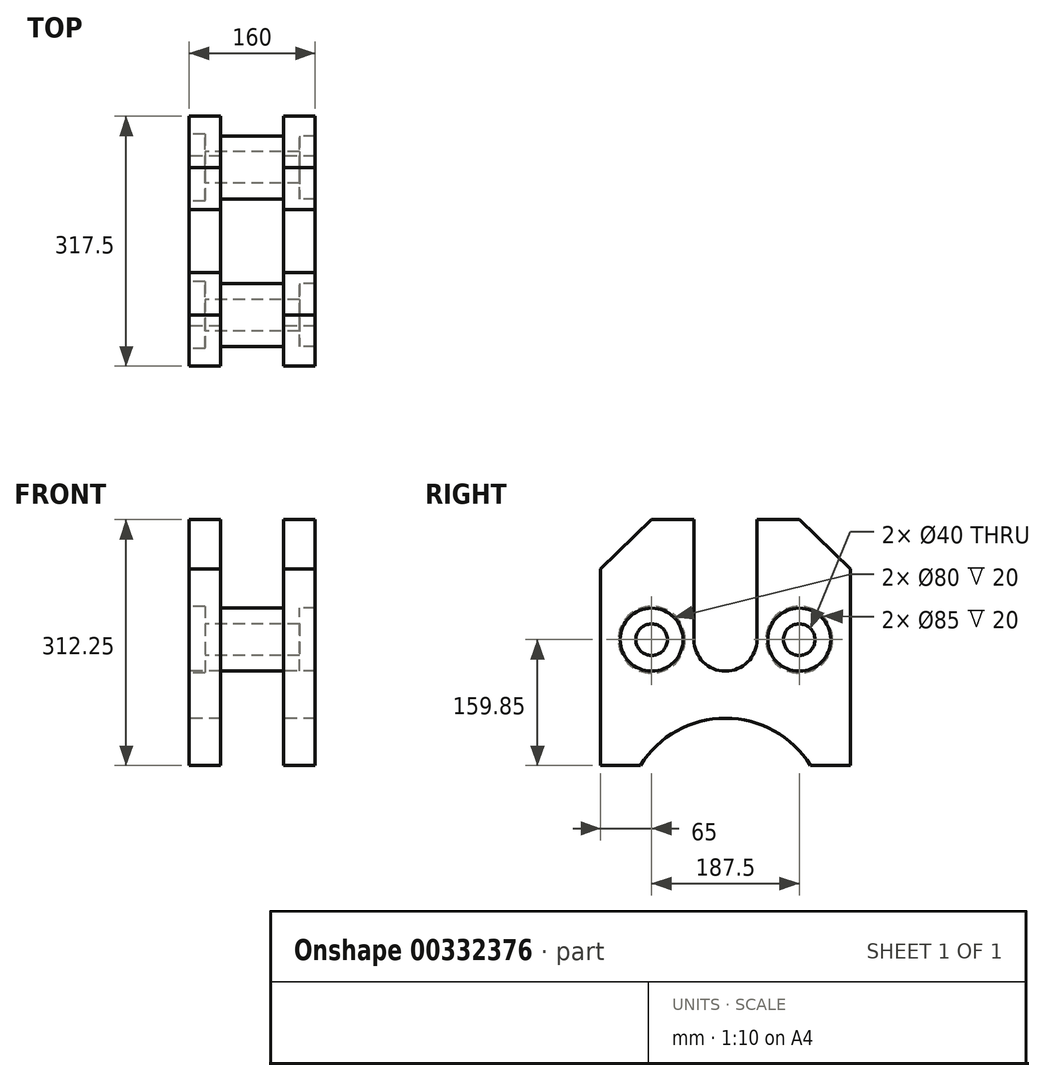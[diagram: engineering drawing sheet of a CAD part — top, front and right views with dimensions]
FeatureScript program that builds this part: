
annotation { "Feature Type Name" : "Feature", "Feature Type Description" : "" }
export const myFeature = defineFeature(function(context is Context, id is Id, definition is map)
    precondition{}
    {
        {
            var Q0;
            Q0=qCreatedBy(makeId("Right.planeOp"),FACE);
            var sketch = newSketch(context, id + "F0", { "sketchPlane" : qUnion([Q0])});
            skLineSegment(sketch, "E0", {"start": v(-158.75, 0) * mm, "end": v(-158.75, 250) * mm});
            skLineSegment(sketch, "E1", {"start": v(-158.75, 250) * mm, "end": v(-93.75, 312.25) * mm});
            skLineSegment(sketch, "E2.MirrorCS", {"start": v(158.75, 250) * mm, "end": v(93.75, 312.25) * mm});
            skLineSegment(sketch, "E3.MirrorCS", {"start": v(158.75, 0) * mm, "end": v(158.75, 250) * mm});
            skLineSegment(sketch, "E4", {"start": v(-158.75, 0) * mm, "end": v(-107.95, 0) * mm});
            skArc(sketch, "E5", {"start": v(107.95, 0) * mm, "mid": v(0, 60.1) * mm, "end": v(-107.95, 0) * mm});
            skLineSegment(sketch, "E6", {"start": v(107.95, 0) * mm, "end": v(158.75, 0) * mm});
            skLineSegment(sketch, "E7", {"start": v(-93.75, 312.25) * mm, "end": v(-40, 312.25) * mm});
            skLineSegment(sketch, "E8", {"start": v(-40, 312.25) * mm, "end": v(-40, 159.85) * mm});
            skArc(sketch, "E9", {"start": v(-40, 159.85) * mm, "mid": v(0, 119.85) * mm, "end": v(40, 159.85) * mm});
            skLineSegment(sketch, "E10", {"start": v(40, 159.85) * mm, "end": v(40, 312.25) * mm});
            skLineSegment(sketch, "E11", {"start": v(40, 312.25) * mm, "end": v(93.75, 312.25) * mm});
            skCircle(sketch, "E12", {"center": v(93.75, 159.85) * mm, "radius": 40 * mm});
            skCircle(sketch, "E13", {"center": v(-93.75, 159.85) * mm, "radius": 40 * mm});
            skSolve(sketch);
        }
        {
            var Q0;
            Q0=makeQuery(id+"F0.imprint","IMPRINT",FACE,{"disambiguationData":[TD([[makeQuery(id+"F0.imprint","IMPRINT",EDGE,{"derivedFrom":sQuery(id+"F0.wireOp",EDGE,"E0")}),-1.0]])]});
            extrude(context, id + "F1", {"entities" : qUnion([Q0]), "endBound" : BoundingType.SYMMETRIC, "depth" : 160 * mm});
        }
        {
            var Q0;
            Q0=makeQuery(id+"F1.opExtrude","SWEPT_FACE",FACE,{"disambiguationData":[OSD([sQuery(id+"F0.wireOp",EDGE,"E3.MirrorCS")])]});
            var sketch = newSketch(context, id + "F2", { "sketchPlane" : qUnion([Q0])});
            skLineSegment(sketch, "E14.bottom", {"start": v(-40, 0) * mm, "end": v(40, 0) * mm});
            skLineSegment(sketch, "E14.top", {"start": v(-40, 330.24) * mm, "end": v(40, 330.24) * mm});
            skLineSegment(sketch, "E14.left", {"start": v(-40, 0) * mm, "end": v(-40, 330.24) * mm});
            skLineSegment(sketch, "E14.right", {"start": v(40, 0) * mm, "end": v(40, 330.24) * mm});
            skSolve(sketch);
        }
        {
            var Q0;
            {var subQ0=sQuery(id+"F2.wireOp",EDGE,"E14.bottom");Q0=makeQuery(id+"F2.imprint","IMPRINT",FACE,{"disambiguationData":[TD([[makeQuery(id+"F2.imprint","IMPRINT",EDGE,{"derivedFrom":subQ0}),1.0]])]});}
            var Q1;
            {var subQ0=sQuery(id+"F2.wireOp",EDGE,"E14.top");Q1=makeQuery(id+"F2.imprint","IMPRINT",FACE,{"disambiguationData":[TD([[makeQuery(id+"F2.imprint","IMPRINT",EDGE,{"derivedFrom":subQ0}),-1.0]])]});}
            var Q2;
            Q2 = qSketchRegion(id + "F4", true);
            extrude(context, id + "F3", {"entities" : qUnion([Q0, Q1, Q2]), "operationType" : NewBodyOperationType.REMOVE, "oppositeDirection" : true, "depth" : 414.02 * mm});
        }
        {
            var Q0;
            Q0=makeQuery(id+"F1.opExtrude","CAP_FACE",FACE,{"disambiguationData":[OSD([sQuery(id+"F0.wireOp",EDGE,"E0"),sQuery(id+"F0.wireOp",EDGE,"E1"),sQuery(id+"F0.wireOp",EDGE,"E2.MirrorCS"),sQuery(id+"F0.wireOp",EDGE,"E3.MirrorCS"),sQuery(id+"F0.wireOp",EDGE,"E4"),sQuery(id+"F0.wireOp",EDGE,"E5"),sQuery(id+"F0.wireOp",EDGE,"E6"),sQuery(id+"F0.wireOp",EDGE,"E7"),sQuery(id+"F0.wireOp",EDGE,"E8"),sQuery(id+"F0.wireOp",EDGE,"E9"),sQuery(id+"F0.wireOp",EDGE,"E10"),sQuery(id+"F0.wireOp",EDGE,"E11"),sQuery(id+"F0.wireOp",EDGE,"E12"),sQuery(id+"F0.wireOp",EDGE,"E13")])],"isStart":true});
            var sketch = newSketch(context, id + "F4", { "sketchPlane" : qUnion([Q0])});
            skCircle(sketch, "E15", {"center": v(-93.75, 159.85) * mm, "radius": 42.5 * mm});
            skCircle(sketch, "E16", {"center": v(-93.75, 159.85) * mm, "radius": 20 * mm});
            skCircle(sketch, "E17", {"center": v(93.75, 159.85) * mm, "radius": 42.5 * mm});
            skCircle(sketch, "E18", {"center": v(93.75, 159.85) * mm, "radius": 20 * mm});
            skSolve(sketch);
        }
        {
            var Q0;
            Q0=makeQuery(id+"F4.imprint","IMPRINT",FACE,{"disambiguationData":[TD([[makeQuery(id+"F4.imprint","IMPRINT",EDGE,{"derivedFrom":sQuery(id+"F4.wireOp",EDGE,"E16")}),-1.0]])]});
            var Q1;
            Q1=makeQuery(id+"F4.imprint","IMPRINT",FACE,{"disambiguationData":[TD([[makeQuery(id+"F4.imprint","IMPRINT",EDGE,{"derivedFrom":sQuery(id+"F4.wireOp",EDGE,"E18")}),-1.0]])]});
            extrude(context, id + "F5", {"entities" : qUnion([Q0, Q1]), "operationType" : NewBodyOperationType.ADD, "oppositeDirection" : true, "depth" : 140 * mm});
        }
        {
            var Q0;
            {var subQ0=sQuery(id+"F0.wireOp",EDGE,"E13");var subQ1=sQuery(id+"F0.wireOp",EDGE,"E12");Q0=makeQuery(id+"F5.boolean.opBoolean","MERGE",FACE,{"derivedFrom":[makeQuery(id+"F1.opExtrude","CAP_FACE",FACE,{"disambiguationData":[OSD([sQuery(id+"F0.wireOp",EDGE,"E0"),sQuery(id+"F0.wireOp",EDGE,"E1"),sQuery(id+"F0.wireOp",EDGE,"E2.MirrorCS"),sQuery(id+"F0.wireOp",EDGE,"E3.MirrorCS"),sQuery(id+"F0.wireOp",EDGE,"E4"),sQuery(id+"F0.wireOp",EDGE,"E5"),sQuery(id+"F0.wireOp",EDGE,"E6"),sQuery(id+"F0.wireOp",EDGE,"E7"),sQuery(id+"F0.wireOp",EDGE,"E8"),sQuery(id+"F0.wireOp",EDGE,"E9"),sQuery(id+"F0.wireOp",EDGE,"E10"),sQuery(id+"F0.wireOp",EDGE,"E11"),subQ1,subQ0])],"isStart":true}),makeQuery(id+"F5.opExtrude","CAP_FACE",FACE,{"disambiguationData":[OSD([subQ1,sQuery(id+"F4.wireOp",EDGE,"E16")])],"isStart":true}),makeQuery(id+"F5.opExtrude","CAP_FACE",FACE,{"disambiguationData":[OSD([subQ0,sQuery(id+"F4.wireOp",EDGE,"E18")])],"isStart":true})]});}
            var sketch = newSketch(context, id + "F6", { "sketchPlane" : qUnion([Q0])});
            skCircle(sketch, "E19", {"center": v(-93.75, 159.85) * mm, "radius": 42.5 * mm});
            skCircle(sketch, "E20", {"center": v(93.75, 159.85) * mm, "radius": 42.5 * mm});
            skSolve(sketch);
        }
        {
            var Q0;
            Q0=makeQuery(id+"F6.imprint","IMPRINT",FACE,{"disambiguationData":[TD([[makeQuery(id+"F6.imprint","IMPRINT",EDGE,{"derivedFrom":sQuery(id+"F6.wireOp",EDGE,"E19")}),1.0]])]});
            var Q1;
            Q1=makeQuery(id+"F6.imprint","IMPRINT",FACE,{"disambiguationData":[TD([[makeQuery(id+"F6.imprint","IMPRINT",EDGE,{"derivedFrom":sQuery(id+"F6.wireOp",EDGE,"E20")}),1.0]])]});
            extrude(context, id + "F7", {"entities" : qUnion([Q0, Q1]), "operationType" : NewBodyOperationType.REMOVE, "oppositeDirection" : true, "depth" : 20 * mm});
        }
    });
